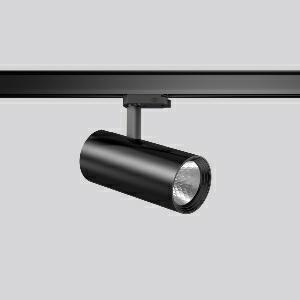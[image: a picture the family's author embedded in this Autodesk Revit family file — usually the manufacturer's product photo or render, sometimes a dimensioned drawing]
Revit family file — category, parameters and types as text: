
# Revit family: deecos_s_mini_742204_003_76_82a4
name_source: partatom
category: Lighting Fixtures
units: mm (PartAtom-declared; Revit-internal decimal feet)

## family parameters
Cut with Voids When Loaded = No
Host = Face
Light Source = No
Part Type = Normal
Room Calculation Point = No
Round Connector Dimension = Use Diameter
Shared = No

## types (1)
- DEECOS S mini (1 x LED Modul 930, 3500 lm, 3000)
    Apparent Load = 29 VA
    Approval mark = CE
    CIE Flux Codes = 99 100 100 100 100
    Color Rendering = 90
    Color Temperature = 3000
    Default Elevation = 1800 mm
    Description = Series: DEECOS S mini
LED surface-mounted projector in modern design with no visible cooling ribs. Housing: die-cast aluminium, powder-coated. Rotation range: 356°. Swivel range: 90°. Black plastic ring and recessed LED to prevent glare from the side. Optical assembly with reflector made of MIRO-Silver with 98% total light reflection for outstanding efficiency - can be changed without tools. Best colour rendering index Ra>90. With adapter for RZB 3-circuit DALI tracks. Suitable for Track on ceiling, Wall track. High quality converter without flickering and stroboscopic effect. The following accessories can be mounted without use of tools: interchangeable lenses, decorative glasses, honeycomb louvre, clear and frosted diffusers, white interchangeable plastic ring. 
Colour: deep black, matt (RAL 9005)
Diameter: 87 mm
Height: 214 mm
Lamp: LED
Socket: without socket
Colour temperature: 3000K
Colour rendering index (CRI): 92
System power: 29 W
Rated luminous flux: 3500 lm
Luminous efficiency: 121 lm/W
Control gear: Converter, dimmable, DALI
Protection class: I
Type of protection: IP 20
    Height = 214 mm
    Lamp = 1 x LED Modul 930
    Lamp Light Flux = 3500 lm
    Lamp count = 1
    Length = 87 mm
    Lifetime = 50000 h
    Luminous efficacy = 121 lm/W
    Manufacturer = RZB
    ModVariant = No
    Model = 742204.003.76
    Mounting Place = Ceiling
    Mounting Type = Rail mounted
    Number of Poles = 1
    OnlyDefault = Yes
    Power Factor = 1
    Product Name = DEECOS S mini
    Product group = Track mounted projectors
    ProductGroupID = 301
    Protection Class = Protection class I
    Protection Degree = IP 20
    RLX_Detail_Level = 1
    RLX_Emergency_Light_Flux = 0 lm
    RLX_Emergency_Type = 0
    RLX_Emergency_Type_DB = No
    RlxData = <blob elided: 38965 chars, md5=ddb8a3eb>
    Socket = socket
    Standby Power = 0 W
    System Light Flux = 3500 lm
    System Power = 29 W
    Type Comments = Product without accessories
    Type Image = 741926.003.jpg
    URL = http://relux.com
    VarID = ---
    Voltage = 230 V
    Voltage Range = 220-240 V
    Weight = 0.00 kg
    Width = 0 mm  [stored 0 ft]

note: [stored X ft] marks values corroborated as IEEE doubles in the binary element streams (Revit-internal decimal feet)

## geometry (parser evidence)
native form markers: Blend x4, Sweep x12
no freeform markers — native parametric forms only
